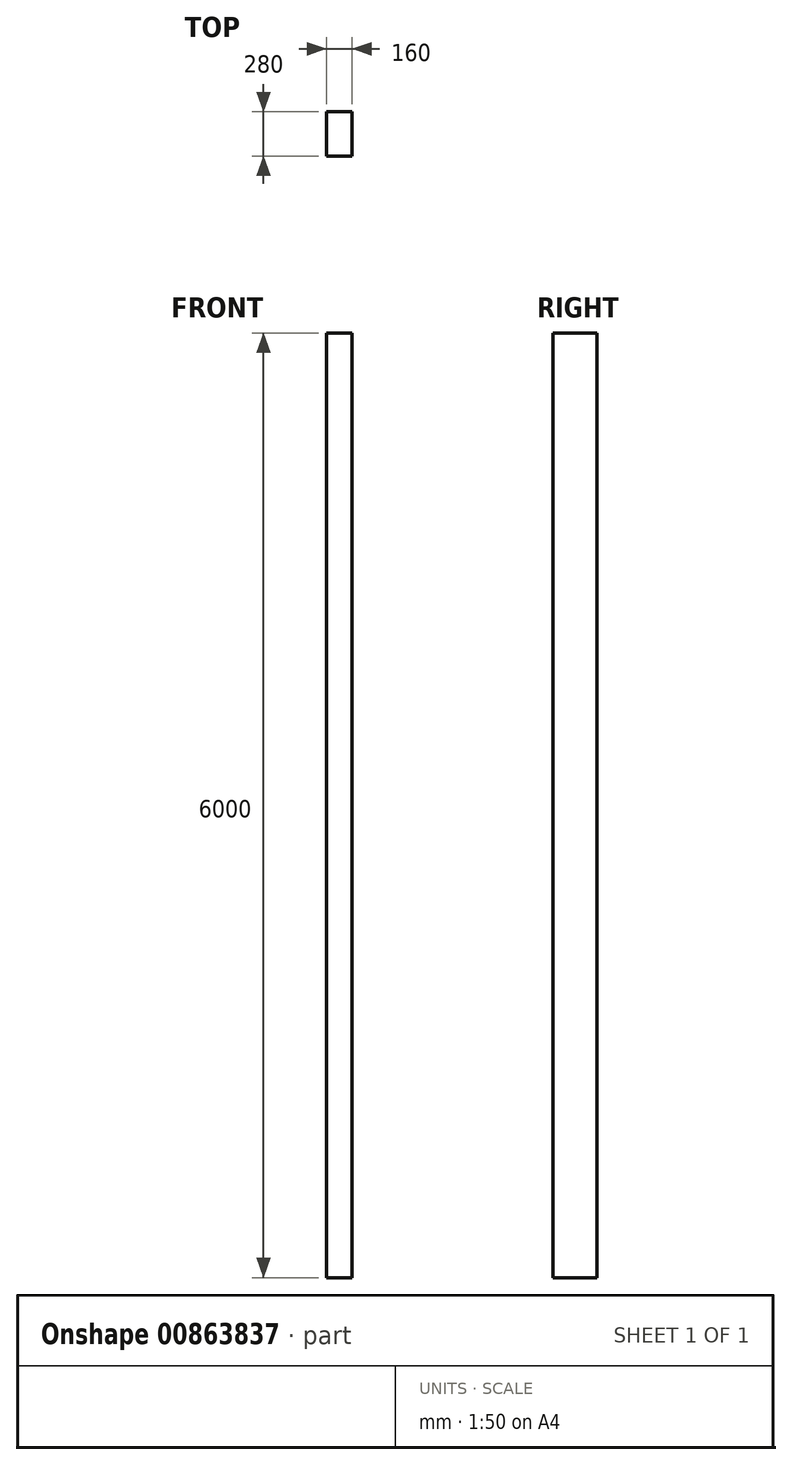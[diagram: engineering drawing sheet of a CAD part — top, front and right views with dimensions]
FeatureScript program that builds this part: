
annotation { "Feature Type Name" : "Feature", "Feature Type Description" : "" }
export const myFeature = defineFeature(function(context is Context, id is Id, definition is map)
    precondition{}
    {
        {
            var Q0;
            Q0=qCreatedBy(makeId("Top.planeOp"),FACE);
            var sketch = newSketch(context, id + "F0", { "sketchPlane" : qUnion([Q0])});
            skLineSegment(sketch, "E0.bottom", {"start": v(-80, -140) * mm, "end": v(80, -140) * mm});
            skLineSegment(sketch, "E0.top", {"start": v(-80, 140) * mm, "end": v(80, 140) * mm});
            skLineSegment(sketch, "E0.left", {"start": v(-80, -140) * mm, "end": v(-80, 140) * mm});
            skLineSegment(sketch, "E0.right", {"start": v(80, -140) * mm, "end": v(80, 140) * mm});
            skPoint(sketch, "E0.middle", {"position": v(0, 0) * mm});
            skSolve(sketch);
        }
        {
            var Q0;
            Q0=makeQuery(id+"F0.imprint","IMPRINT",FACE,{"disambiguationData":[TD([[makeQuery(id+"F0.imprint","IMPRINT",EDGE,{"derivedFrom":sQuery(id+"F0.wireOp",EDGE,"E0.bottom")}),1.0]])]});
            extrude(context, id + "F1", {"entities" : qUnion([Q0]), "endBound" : BoundingType.SYMMETRIC, "depth" : 6000 * mm, "offsetDistance" : 25 * mm});
        }
    });
